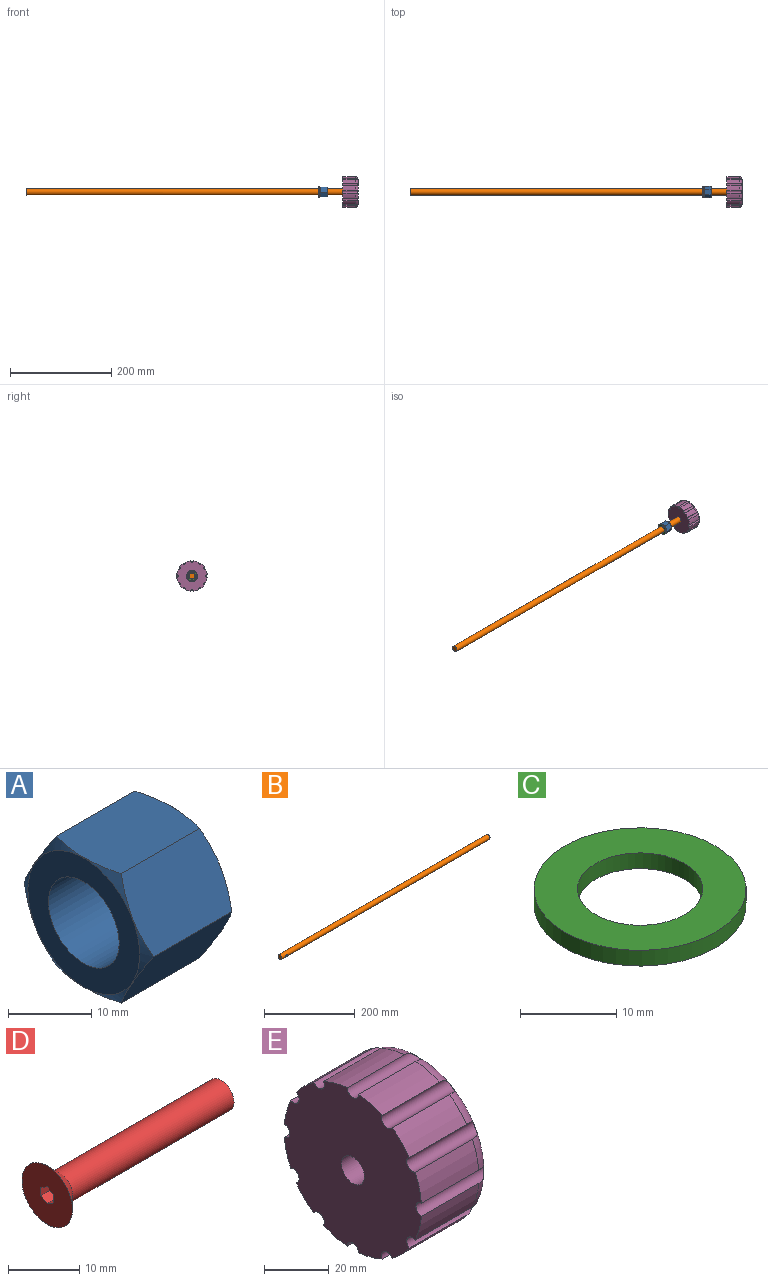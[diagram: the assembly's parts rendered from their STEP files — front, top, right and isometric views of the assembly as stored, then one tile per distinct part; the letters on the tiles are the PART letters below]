
ASSEMBLY  parts=5 mates=4
PART A: 11 faces, bbox 15x21.9x21.9 mm
  f0: plane 18.94x18.94mm, normal (1,0,0), area 168.6mm2, adj f1,f4
  f1: cylinder r=6mm len=15mm, axis (-1,0,0), area 565.5mm2, adj f0,f2
  f2: plane 18.94x18.94mm, normal (-1,0,0), area 168.6mm2, adj f1,f3
  f3: cone r=9.47mm half-angle=60deg, axis (1,0,0), area 35.7mm2, adj f2,f5,f6,f7,f8,f9,f10
  f4: cone r=9.47mm half-angle=60deg, axis (-1,0,0), area 35.7mm2, adj f0,f5,f6,f7,f8,f9,f10
  f5: plane 14.97x9.5mm, normal (0,-0.87,-0.5), area 157.8mm2, adj f3,f4,f6,f10
  f6: plane 14.97x9.5mm, normal (0,-0.87,0.5), area 157.8mm2, adj f3,f4,f5,f7
  f7: plane 14.97x10.98mm, normal (0,0,1), area 157.8mm2, adj f3,f4,f6,f8
  f8: plane 14.97x9.5mm, normal (0,0.87,0.5), area 157.8mm2, adj f3,f4,f7,f9
  f9: plane 14.97x9.5mm, normal (0,0.87,-0.5), area 157.8mm2, adj f3,f4,f8,f10
  f10: plane 14.97x10.98mm, normal (0,0,-1), area 157.8mm2, adj f3,f4,f5,f9
PART B: 4 faces, bbox 650x12x12 mm
  f0: cylinder r=6mm len=650mm, axis (-1,0,0), area 24464.2mm2, adj f1,f2,f3
  f1: plane 12x12mm, normal (1,0,0), area 113.1mm2, adj f0
  f2: plane 12x12mm, normal (-1,0,0), area 113.1mm2, adj f0
  f3: cylinder r=2.5mm len=12mm, axis (0,-1,0), area 180mm2, adj f0
PART C: 4 faces, bbox 22x22x2 mm
  f0: cylinder r=6.5mm len=13mm, axis (0,0,-1), area 81.7mm2, adj f2,f3
  f1: cylinder r=11mm len=22mm, axis (0,0,-1), area 138.2mm2, adj f2,f3
  f2: plane 22x22mm, normal (0,0,1), area 247.4mm2, adj f0,f1
  f3: plane 22x22mm, normal (0,0,-1), area 247.4mm2, adj f0,f1
PART D: 11 faces, bbox 34.5x10x10 mm
  f0: plane 10x10mm, normal (-1,0,0), area 73.1mm2, adj f3,f4,f5,f6,f7,f8,f9
  f1: plane 5x5mm, normal (1,0,0), area 19.6mm2, adj f2
  f2: cylinder r=2.5mm len=32mm, axis (-1,0,0), area 502.7mm2, adj f1,f3
  f3: cone r=5mm half-angle=45deg, axis (-1,0,0), area 83.3mm2, adj f0,f2
  f4: plane 2x1.25mm, normal (0,0.5,0.87), area 2.9mm2, adj f0,f5,f9,f10
  f5: plane 2x1.44mm, normal (0,1,0), area 2.9mm2, adj f0,f4,f6,f10
  f6: plane 2x1.25mm, normal (0,0.5,-0.87), area 2.9mm2, adj f0,f5,f7,f10
  f7: plane 2x1.25mm, normal (0,-0.5,-0.87), area 2.9mm2, adj f0,f6,f8,f10
  f8: plane 2x1.44mm, normal (0,-1,0), area 2.9mm2, adj f0,f7,f9,f10
  f9: plane 2x1.25mm, normal (0,-0.5,0.87), area 2.9mm2, adj f0,f4,f8,f10
  f10: plane 2.89x2.5mm, normal (-1,0,0), area 5.4mm2, adj f4,f5,f6,f7,f8,f9
PART E: 34 faces, bbox 30x64.9x64.9 mm
  f0: cylinder r=2.5mm len=6.9mm, axis (-1,0,0), area 49.2mm2, adj f1,f2,f14,f31,f32,f33
  f1: cylinder r=30mm len=25mm, axis (-1,0,0), area 252.2mm2, adj f0,f3,f14,f17,f25,f31
  f2: cylinder r=30mm len=25mm, axis (-1,0,0), area 252.2mm2, adj f0,f3,f14,f17,f24,f32
  f3: cylinder r=2.5mm len=16.23mm, axis (-1,0,0), area 113.7mm2, adj f1,f2,f17,f31,f32,f33
  f4: cylinder r=2.75mm len=22.97mm, axis (0,-1,0), area 389.6mm2, adj f18,f33
  f5: cylinder r=30mm len=25mm, axis (-1,0,0), area 267.7mm2, adj f14,f17,f26,f30
  f6: cylinder r=30mm len=25mm, axis (-1,0,0), area 267.7mm2, adj f14,f17,f29,f30
  f7: cylinder r=30mm len=25mm, axis (-1,0,0), area 267.7mm2, adj f14,f17,f28,f29
  f8: cylinder r=30mm len=25mm, axis (-1,0,0), area 267.7mm2, adj f14,f17,f27,f28
  f9: cylinder r=30mm len=25mm, axis (-1,0,0), area 267.7mm2, adj f14,f17,f25,f26
  f10: cylinder r=30mm len=25mm, axis (-1,0,0), area 267.7mm2, adj f14,f17,f23,f24
  f11: cylinder r=30mm len=25mm, axis (-1,0,0), area 267.7mm2, adj f14,f17,f22,f23
  f12: cylinder r=30mm len=25mm, axis (-1,0,0), area 267.7mm2, adj f14,f17,f21,f22
  f13: cylinder r=30mm len=25mm, axis (-1,0,0), area 267.7mm2, adj f14,f17,f20,f21
  f14: plane 59.79x59.79mm, normal (-1,0,0), area 2633.2mm2, adj f0,f1,f2,f5,f6,f7,f8,f9
  f15: cylinder r=30mm len=25mm, axis (-1,0,0), area 267.7mm2, adj f14,f17,f20,f27
  f16: plane 50x50mm, normal (1,0,0), area 1963.5mm2, adj f17
  f17: torus R=25mm, axis (1,0,0), area 1122mm2, adj f1,f2,f3,f5,f6,f7,f8,f9
  f18: cylinder r=5mm len=25mm, axis (-1,0,0), area 760.6mm2, adj f4,f14,f19
  f19: plane 10x10mm, normal (-1,0,0), area 78.5mm2, adj f18
  f20: cylinder r=2.5mm len=29.33mm, axis (-1,0,0), area 217.4mm2, adj f13,f14,f15,f17
  f21: cylinder r=2.5mm len=29.33mm, axis (-1,0,0), area 217.4mm2, adj f12,f13,f14,f17
  f22: cylinder r=2.5mm len=29.33mm, axis (-1,0,0), area 217.4mm2, adj f11,f12,f14,f17
  f23: cylinder r=2.5mm len=29.33mm, axis (-1,0,0), area 217.4mm2, adj f10,f11,f14,f17
  f24: cylinder r=2.5mm len=29.33mm, axis (-1,0,0), area 217.4mm2, adj f2,f10,f14,f17
  f25: cylinder r=2.5mm len=29.33mm, axis (-1,0,0), area 217.4mm2, adj f1,f9,f14,f17
  f26: cylinder r=2.5mm len=29.33mm, axis (-1,0,0), area 217.4mm2, adj f5,f9,f14,f17
  f27: cylinder r=2.5mm len=29.33mm, axis (-1,0,0), area 217.4mm2, adj f8,f14,f15,f17
  f28: cylinder r=2.5mm len=29.33mm, axis (-1,0,0), area 217.4mm2, adj f7,f8,f14,f17
  f29: cylinder r=2.5mm len=29.33mm, axis (-1,0,0), area 217.4mm2, adj f6,f7,f14,f17
  f30: cylinder r=2.5mm len=29.33mm, axis (-1,0,0), area 217.4mm2, adj f5,f6,f14,f17
  f31: cylinder r=5mm len=8.74mm, axis (0,1,0), area 3.3mm2, adj f0,f1,f3,f33
  f32: cylinder r=5mm len=8.74mm, axis (0,1,0), area 3.3mm2, adj f0,f2,f3,f33
  f33: cone r=2.5mm half-angle=45deg, axis (0,1,0), area 57.4mm2, adj f0,f3,f4,f31,f32
PLACE A rot(axis=(0,1,0),180deg) t=(375.42,24.01,-76.93)mm
PLACE B rot(axis=(0,1,0),180deg) t=(430.42,24.01,-76.93)mm
PLACE C rot(axis=(-0.71,0,-0.71),180deg) t=(358.42,24.01,-76.93)mm
PLACE D rot(axis=(-0.58,0.58,-0.58),120deg) t=(415.42,53.65,-76.93)mm
PLACE E t=(405.42,24.01,-76.93)mm
MATE fastened E.f18 <-> B.f0  axis (-1,0,0) through (430.42,24.01,-76.93)mm
MATE revolute C.f0 <-> A.f3  axis (1,0,0) through (360.42,24.01,-76.93)mm
MATE fastened D.f2 <-> E.f4  axis (0,1,0) through (415.42,51.15,-76.93)mm
MATE fastened A.f3 <-> E.f1  axis (1,0,0) through (375.42,24.01,-76.93)mm
